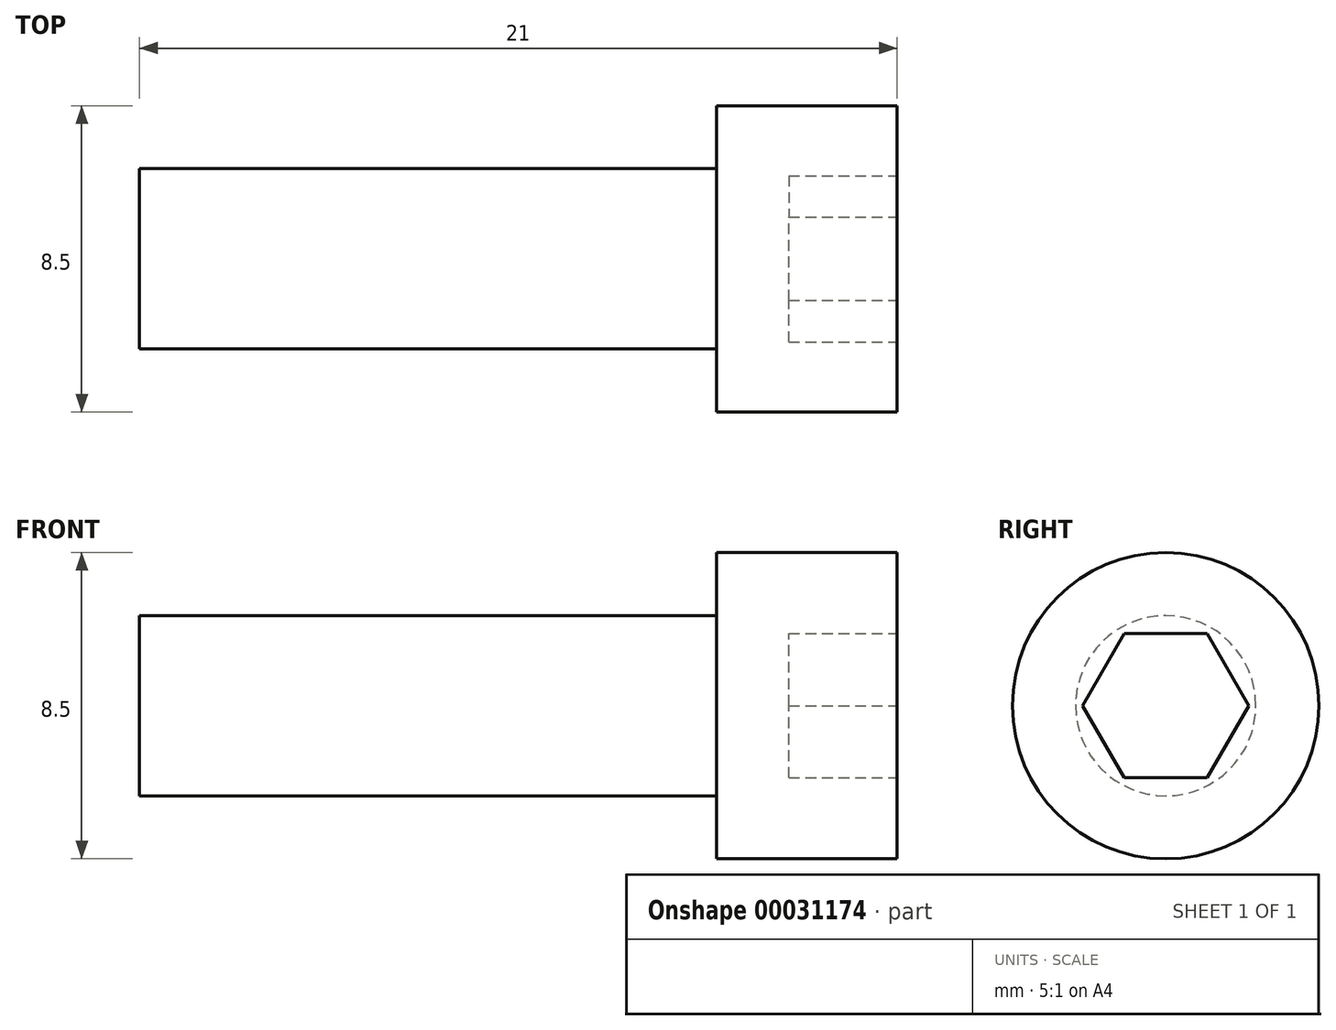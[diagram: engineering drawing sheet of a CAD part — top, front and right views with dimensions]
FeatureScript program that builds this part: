
annotation { "Feature Type Name" : "Feature", "Feature Type Description" : "" }
export const myFeature = defineFeature(function(context is Context, id is Id, definition is map)
    precondition{}
    {
        {
            var Q0;
            Q0=qCreatedBy(makeId("Right.planeOp"),FACE);
            var sketch = newSketch(context, id + "F0", { "sketchPlane" : qUnion([Q0])});
            skCircle(sketch, "E0", {"center": v(0, 0) * mm, "radius": 4.25 * mm});
            skSolve(sketch);
        }
        {
            var Q0;
            Q0 = qSketchRegion(id + "F0", true);
            extrude(context, id + "F1", {"entities" : qUnion([Q0]), "depth" : 5 * mm});
        }
        {
            var Q0;
            Q0=makeQuery(id+"F1.opExtrude","CAP_FACE",FACE,{"disambiguationData":[OSD([sQuery(id+"F0.wireOp",EDGE,"E0")])],"isStart":true});
            var sketch = newSketch(context, id + "F2", { "sketchPlane" : qUnion([Q0])});
            skCircle(sketch, "E1", {"center": v(0, 0) * mm, "radius": 2.5 * mm});
            skSolve(sketch);
        }
        {
            var Q0;
            Q0 = qSketchRegion(id + "F2", true);
            extrude(context, id + "F3", {"entities" : qUnion([Q0]), "operationType" : NewBodyOperationType.ADD, "depth" : 16 * mm});
        }
        {
            var Q0;
            Q0=makeQuery(id+"F1.opExtrude","CAP_FACE",FACE,{"disambiguationData":[OSD([sQuery(id+"F0.wireOp",EDGE,"E0")])],"isStart":false});
            var sketch = newSketch(context, id + "F4", { "sketchPlane" : qUnion([Q0])});
            skCircle(sketch, "E2.cCircle", {"center": v(0, 0) * mm, "radius": 2 * mm, "construction": true});
            skLineSegment(sketch, "E2.0", {"start": v(-1.15, 2) * mm, "end": v(1.15, 2) * mm});
            skLineSegment(sketch, "E2.1", {"start": v(1.15, 2) * mm, "end": v(2.3, 0) * mm});
            skLineSegment(sketch, "E2.2", {"start": v(2.3, 0) * mm, "end": v(1.15, -2) * mm});
            skLineSegment(sketch, "E2.3", {"start": v(1.15, -2) * mm, "end": v(-1.15, -2) * mm});
            skLineSegment(sketch, "E2.4", {"start": v(-1.15, -2) * mm, "end": v(-2.3, 0) * mm});
            skLineSegment(sketch, "E2.5", {"start": v(-2.3, 0) * mm, "end": v(-1.15, 2) * mm});
            skPoint(sketch, "E2.0.midPoint", {"position": v(0, 2) * mm});
            skSolve(sketch);
        }
        {
            var Q0;
            Q0 = qSketchRegion(id + "F4", true);
            extrude(context, id + "F5", {"entities" : qUnion([Q0]), "operationType" : NewBodyOperationType.REMOVE, "oppositeDirection" : true, "depth" : 3 * mm});
        }
    });
